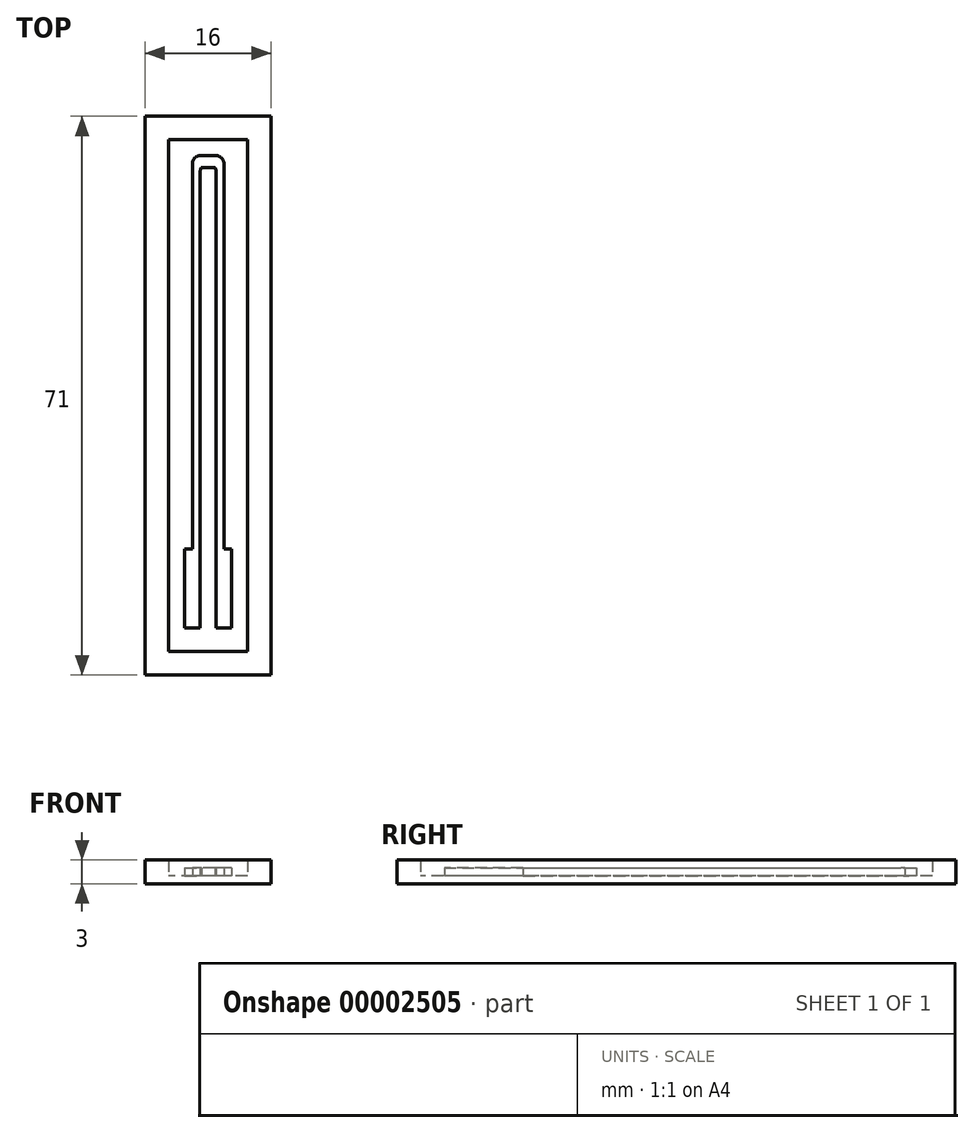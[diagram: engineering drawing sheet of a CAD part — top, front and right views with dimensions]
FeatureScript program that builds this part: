
annotation { "Feature Type Name" : "Feature", "Feature Type Description" : "" }
export const myFeature = defineFeature(function(context is Context, id is Id, definition is map)
    precondition{}
    {
        {
            var Q0;
            Q0=qCreatedBy(makeId("Top.planeOp"),FACE);
            var sketch = newSketch(context, id + "F0", { "sketchPlane" : qUnion([Q0])});
            skLineSegment(sketch, "E0.rect.bottom", {"start": v(5, 32.5) * mm, "end": v(-5, 32.5) * mm});
            skLineSegment(sketch, "E0.rect.top", {"start": v(5, -32.5) * mm, "end": v(-5, -32.5) * mm});
            skLineSegment(sketch, "E0.rect.left", {"start": v(5, 32.5) * mm, "end": v(5, -32.5) * mm});
            skLineSegment(sketch, "E0.rect.right", {"start": v(-5, 32.5) * mm, "end": v(-5, -32.5) * mm});
            skPoint(sketch, "E0.rect.middle", {"position": v(0, 0) * mm});
            skLineSegment(sketch, "E1", {"start": v(0, 0) * mm, "end": v(0, 17.9) * mm, "construction": true});
            skLineSegment(sketch, "E2.bottom", {"start": v(-3, -19.5) * mm, "end": v(-2, -19.5) * mm});
            skLineSegment(sketch, "E2.top", {"start": v(-3, -29.5) * mm, "end": v(-1, -29.5) * mm});
            skLineSegment(sketch, "E2.left", {"start": v(-3, -19.5) * mm, "end": v(-3, -29.5) * mm});
            skLineSegment(sketch, "E2.right", {"start": v(-1, -19.5) * mm, "end": v(-1, -29.5) * mm});
            skLineSegment(sketch, "E3", {"start": v(-1, -19.5) * mm, "end": v(-1, 28.5) * mm});
            skLineSegment(sketch, "E4", {"start": v(0, 29.5) * mm, "end": v(0, 29.5) * mm});
            skLineSegment(sketch, "E5", {"start": v(-2, -19.5) * mm, "end": v(-2, 29.5) * mm});
            skLineSegment(sketch, "E6", {"start": v(-1, 30.5) * mm, "end": v(0, 30.5) * mm});
            skPoint(sketch, "E7.visualSharp", {"position": v(-2, 30.5) * mm});
            skArc(sketch, "E7.filletArc", {"start": v(-1, 30.5) * mm, "mid": v(-1.7, 30.2) * mm, "end": v(-2, 29.5) * mm});
            skArc(sketch, "E8.filletArc", {"start": v(0, 29.5) * mm, "mid": v(-0.7, 29.2) * mm, "end": v(-1, 28.5) * mm});
            skLineSegment(sketch, "E9.0.MirrorCS", {"start": v(3, -29.5) * mm, "end": v(1, -29.5) * mm});
            skArc(sketch, "E9.1.MirrorCS", {"start": v(0, 29.5) * mm, "mid": v(0.7, 29.2) * mm, "end": v(1, 28.5) * mm});
            skArc(sketch, "E9.2.MirrorCS", {"start": v(1, 30.5) * mm, "mid": v(1.7, 30.2) * mm, "end": v(2, 29.5) * mm});
            skLineSegment(sketch, "E9.3.MirrorCS", {"start": v(3, -19.5) * mm, "end": v(2, -19.5) * mm});
            skLineSegment(sketch, "E9.5.MirrorCS", {"start": v(1, 30.5) * mm, "end": v(0, 30.5) * mm});
            skPoint(sketch, "E9.6.MirrorP", {"position": v(2, 30.5) * mm});
            skLineSegment(sketch, "E9.8.MirrorCS", {"start": v(1, -19.5) * mm, "end": v(1, -29.5) * mm});
            skPoint(sketch, "E9.9.MirrorP", {"position": v(1, 29.5) * mm});
            skLineSegment(sketch, "E9.10.MirrorCS", {"start": v(2, -19.5) * mm, "end": v(2, 29.5) * mm});
            skLineSegment(sketch, "E9.11.MirrorCS", {"start": v(3, -19.5) * mm, "end": v(3, -29.5) * mm});
            skLineSegment(sketch, "E9.12.MirrorCS", {"start": v(1, -19.5) * mm, "end": v(1, 28.5) * mm});
            skLineSegment(sketch, "E10.0", {"start": v(8, 35.5) * mm, "end": v(-8, 35.5) * mm});
            skLineSegment(sketch, "E10.1", {"start": v(8, 35.5) * mm, "end": v(8, -35.5) * mm});
            skLineSegment(sketch, "E10.2", {"start": v(8, -35.5) * mm, "end": v(-8, -35.5) * mm});
            skLineSegment(sketch, "E10.3", {"start": v(-8, 35.5) * mm, "end": v(-8, -35.5) * mm});
            skSolve(sketch);
        }
        {
            var Q0;
            Q0=makeQuery(id+"F0.imprint","IMPRINT",FACE,{"disambiguationData":[TD([[makeQuery(id+"F0.imprint","IMPRINT",EDGE,{"derivedFrom":sQuery(id+"F0.wireOp",EDGE,"E0.rect.bottom")}),-1.0]])]});
            extrude(context, id + "F1", {"entities" : qUnion([Q0]), "depth" : 2 * mm});
        }
        {
            var Q0;
            Q0=makeQuery(id+"F0.imprint","IMPRINT",FACE,{"disambiguationData":[TD([[makeQuery(id+"F0.imprint","IMPRINT",EDGE,{"derivedFrom":sQuery(id+"F0.wireOp",EDGE,"E0.rect.bottom")}),1.0]])]});
            var Q1;
            Q1=makeQuery(id+"F1.opExtrude","CAP_FACE",FACE,{"disambiguationData":[OSD([sQuery(id+"F0.wireOp",EDGE,"E0.rect.bottom"),sQuery(id+"F0.wireOp",EDGE,"E0.rect.top"),sQuery(id+"F0.wireOp",EDGE,"E0.rect.left"),sQuery(id+"F0.wireOp",EDGE,"E0.rect.right"),sQuery(id+"F0.wireOp",EDGE,"E10.0"),sQuery(id+"F0.wireOp",EDGE,"E10.1"),sQuery(id+"F0.wireOp",EDGE,"E10.2"),sQuery(id+"F0.wireOp",EDGE,"E10.3")])],"isStart":false});
            var Q2;
            Q2=makeQuery(id+"F0.imprint","IMPRINT",FACE,{"disambiguationData":[TD([[makeQuery(id+"F0.imprint","IMPRINT",EDGE,{"derivedFrom":sQuery(id+"F0.wireOp",EDGE,"E2.bottom")}),-1.0]])]});
            extrude(context, id + "F2", {"entities" : qUnion([Q0, Q1, Q2]), "operationType" : NewBodyOperationType.ADD, "depth" : 1 * mm});
        }
        {
            var Q0;
            Q0=makeQuery(id+"F2.opExtrude","CAP_FACE",FACE,{"disambiguationData":[OSD([sQuery(id+"F0.wireOp",EDGE,"E0.rect.bottom"),sQuery(id+"F0.wireOp",EDGE,"E0.rect.top"),sQuery(id+"F0.wireOp",EDGE,"E0.rect.left"),sQuery(id+"F0.wireOp",EDGE,"E0.rect.right")])],"isStart":false});
            var sketch = newSketch(context, id + "F3", { "sketchPlane" : qUnion([Q0])});
            skLineSegment(sketch, "E11.0", {"start": v(-3, -19.5) * mm, "end": v(-3, -29.5) * mm});
            skLineSegment(sketch, "E12.0", {"start": v(-3, -29.5) * mm, "end": v(-1, -29.5) * mm});
            skLineSegment(sketch, "E13.0", {"start": v(-1, -19.5) * mm, "end": v(-1, -29.5) * mm});
            skLineSegment(sketch, "E14.0", {"start": v(-3, -19.5) * mm, "end": v(-2, -19.5) * mm});
            skLineSegment(sketch, "E15.0", {"start": v(-2, -19.5) * mm, "end": v(-2, 29.5) * mm});
            skLineSegment(sketch, "E16.0", {"start": v(-1, -19.5) * mm, "end": v(-1, 28.5) * mm});
            skArc(sketch, "E17.0", {"start": v(-1, 30.5) * mm, "mid": v(-1.7, 30.2) * mm, "end": v(-2, 29.5) * mm});
            skArc(sketch, "E18.0", {"start": v(0, 29.5) * mm, "mid": v(-0.7, 29.2) * mm, "end": v(-1, 28.5) * mm});
            skLineSegment(sketch, "E19.0", {"start": v(-4, 29) * mm, "end": v(0, 29) * mm});
            skLineSegment(sketch, "E20.0", {"start": v(-1, 30.5) * mm, "end": v(0, 30.5) * mm});
            skLineSegment(sketch, "E21.0", {"start": v(4, 29) * mm, "end": v(0, 29) * mm});
            skLineSegment(sketch, "E22.0", {"start": v(1, 30.5) * mm, "end": v(0, 30.5) * mm});
            skArc(sketch, "E23.0", {"start": v(0, 29.5) * mm, "mid": v(0.7, 29.2) * mm, "end": v(1, 28.5) * mm});
            skArc(sketch, "E24.0", {"start": v(1, 30.5) * mm, "mid": v(1.7, 30.2) * mm, "end": v(2, 29.5) * mm});
            skLineSegment(sketch, "E25.0", {"start": v(1, -19.5) * mm, "end": v(1, 28.5) * mm});
            skLineSegment(sketch, "E26.0", {"start": v(2, -19.5) * mm, "end": v(2, 29.5) * mm});
            skLineSegment(sketch, "E27.0", {"start": v(1, -19.5) * mm, "end": v(1, -29.5) * mm});
            skLineSegment(sketch, "E28.0", {"start": v(3, -29.5) * mm, "end": v(1, -29.5) * mm});
            skLineSegment(sketch, "E29.0", {"start": v(3, -19.5) * mm, "end": v(3, -29.5) * mm});
            skLineSegment(sketch, "E30.0", {"start": v(3, -19.5) * mm, "end": v(2, -19.5) * mm});
            skSolve(sketch);
        }
        {
            var Q0;
            Q0 = qSketchRegion(id + "F3", true);
            extrude(context, id + "F4", {"entities" : qUnion([Q0]), "operationType" : NewBodyOperationType.ADD, "depth" : 1 * mm});
        }
    });
